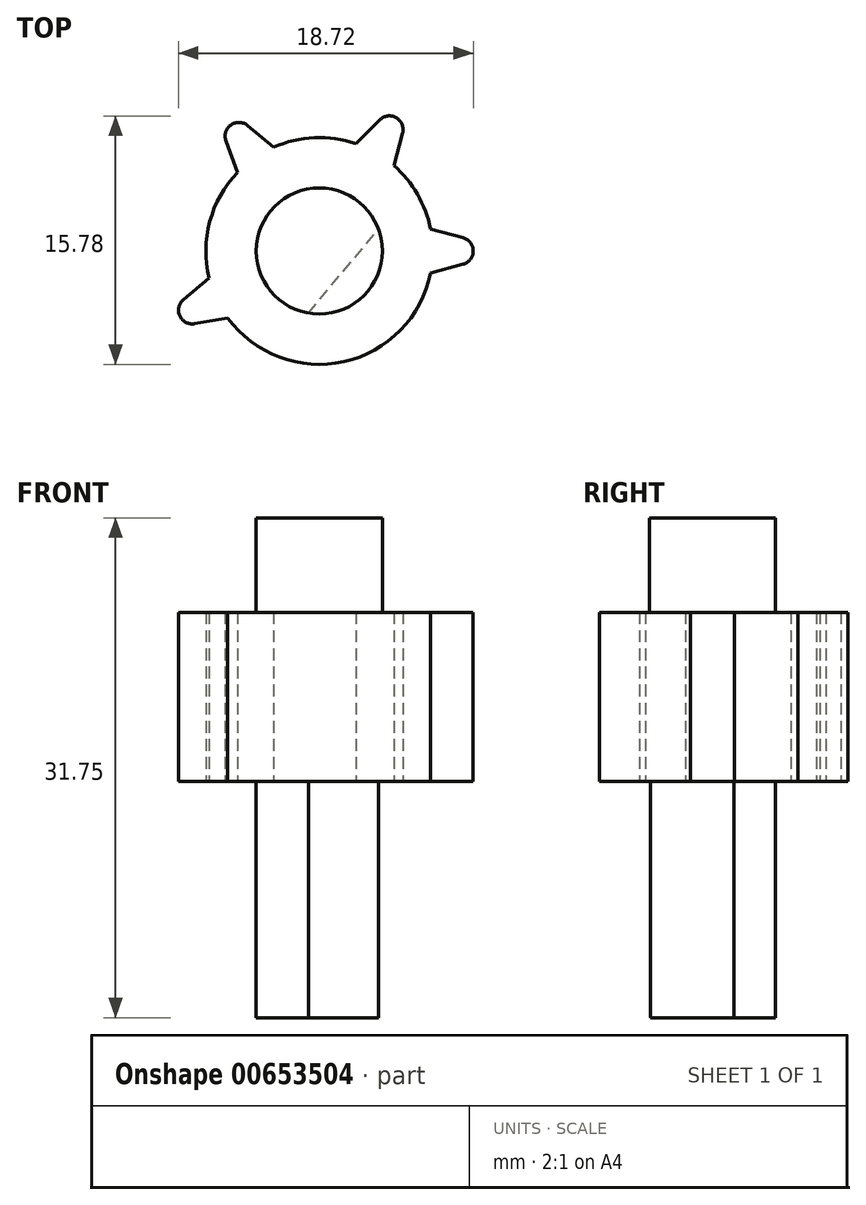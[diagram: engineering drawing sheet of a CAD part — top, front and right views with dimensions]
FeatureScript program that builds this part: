
annotation { "Feature Type Name" : "Feature", "Feature Type Description" : "" }
export const myFeature = defineFeature(function(context is Context, id is Id, definition is map)
    precondition{}
    {
        {
            var Q0;
            Q0=qCreatedBy(makeId("Top.planeOp"),FACE);
            var sketch = newSketch(context, id + "F0", { "sketchPlane" : qUnion([Q0])});
            skCircle(sketch, "E0", {"center": v(0, 0) * mm, "radius": 7.2 * mm});
            skLineSegment(sketch, "E1", {"start": v(0, 0) * mm, "end": v(-8.07, -3.76) * mm});
            skLineSegment(sketch, "E2", {"start": v(0, 0) * mm, "end": v(8.9, 0) * mm});
            skLineSegment(sketch, "E3", {"start": v(0, 0) * mm, "end": v(4.45, 7.7) * mm});
            skLineSegment(sketch, "E4", {"start": v(0, 0) * mm, "end": v(-5.1, 7.3) * mm});
            skCircle(sketch, "E5", {"center": v(-5.1, 7.3) * mm, "radius": 0.88 * mm});
            skCircle(sketch, "E6", {"center": v(4.45, 7.7) * mm, "radius": 0.88 * mm});
            skCircle(sketch, "E7", {"center": v(8.9, 0) * mm, "radius": 0.88 * mm});
            skLineSegment(sketch, "E8", {"start": v(4.45, 7.7) * mm, "end": v(5.2, 7.27) * mm, "construction": true});
            skLineSegment(sketch, "E9", {"start": v(4.45, 7.7) * mm, "end": v(3.7, 8.15) * mm, "construction": true});
            skLineSegment(sketch, "E10", {"start": v(-5.1, 7.3) * mm, "end": v(-4.39, 7.8) * mm, "construction": true});
            skLineSegment(sketch, "E11", {"start": v(-5.1, 7.3) * mm, "end": v(-5.82, 6.79) * mm, "construction": true});
            skLineSegment(sketch, "E12", {"start": v(-5.1, 7.3) * mm, "end": v(-4.54, 7.96) * mm, "construction": true});
            skLineSegment(sketch, "E13", {"start": v(-5.1, 7.3) * mm, "end": v(-5.93, 7) * mm, "construction": true});
            skLineSegment(sketch, "E14", {"start": v(8.9, 0) * mm, "end": v(8.9, -0.88) * mm, "construction": true});
            skLineSegment(sketch, "E15", {"start": v(8.9, 0) * mm, "end": v(8.9, 0.88) * mm, "construction": true});
            skLineSegment(sketch, "E16", {"start": v(8.9, 0) * mm, "end": v(9.13, 0.85) * mm});
            skLineSegment(sketch, "E17", {"start": v(8.9, 0) * mm, "end": v(9.13, -0.85) * mm});
            skLineSegment(sketch, "E18", {"start": v(4.45, 7.7) * mm, "end": v(3.83, 8.33) * mm});
            skLineSegment(sketch, "E19", {"start": v(4.45, 7.7) * mm, "end": v(5.3, 7.48) * mm});
            skLineSegment(sketch, "E20", {"start": v(-5.93, 7) * mm, "end": v(-5.2, 4.98) * mm});
            skLineSegment(sketch, "E21", {"start": v(-4.54, 7.96) * mm, "end": v(-2.9, 6.59) * mm});
            skLineSegment(sketch, "E22", {"start": v(3.83, 8.33) * mm, "end": v(2.32, 6.82) * mm});
            skLineSegment(sketch, "E23", {"start": v(5.3, 7.48) * mm, "end": v(4.74, 5.42) * mm});
            skLineSegment(sketch, "E24", {"start": v(9.13, 0.85) * mm, "end": v(7.06, 1.4) * mm});
            skLineSegment(sketch, "E25", {"start": v(9.13, -0.85) * mm, "end": v(7.06, -1.4) * mm});
            skCircle(sketch, "E26", {"center": v(-8.07, -3.76) * mm, "radius": 0.88 * mm});
            skLineSegment(sketch, "E27", {"start": v(-8.07, -3.76) * mm, "end": v(-8.44, -2.97) * mm, "construction": true});
            skLineSegment(sketch, "E28", {"start": v(-8.07, -3.76) * mm, "end": v(-7.7, -4.55) * mm, "construction": true});
            skLineSegment(sketch, "E29", {"start": v(-8.07, -3.76) * mm, "end": v(-7.91, -4.62) * mm, "construction": true});
            skLineSegment(sketch, "E30", {"start": v(-8.07, -3.76) * mm, "end": v(-8.63, -3.1) * mm, "construction": true});
            skLineSegment(sketch, "E31", {"start": v(-8.63, -3.1) * mm, "end": v(-7, -1.72) * mm});
            skLineSegment(sketch, "E32", {"start": v(-7.91, -4.62) * mm, "end": v(-5.81, -4.25) * mm});
            skSolve(sketch);
        }
        {
            var Q0;
            Q0 = qSketchRegion(id + "F0", true);
            extrude(context, id + "F1", {"entities" : qUnion([Q0]), "depth" : 10.75 * mm, "offsetDistance" : 25 * mm});
        }
        {
            var Q0;
            Q0=makeQuery(id+"F1.opExtrude","CAP_FACE",FACE,{"disambiguationData":[OSD([sQuery(id+"F0.wireOp",EDGE,"E0"),sQuery(id+"F0.wireOp",EDGE,"E5"),sQuery(id+"F0.wireOp",EDGE,"E6"),sQuery(id+"F0.wireOp",EDGE,"E7"),sQuery(id+"F0.wireOp",EDGE,"E20"),sQuery(id+"F0.wireOp",EDGE,"E21"),sQuery(id+"F0.wireOp",EDGE,"E22"),sQuery(id+"F0.wireOp",EDGE,"E23"),sQuery(id+"F0.wireOp",EDGE,"E24"),sQuery(id+"F0.wireOp",EDGE,"E25"),sQuery(id+"F0.wireOp",EDGE,"E26"),sQuery(id+"F0.wireOp",EDGE,"E31"),sQuery(id+"F0.wireOp",EDGE,"E32")])],"isStart":false});
            var sketch = newSketch(context, id + "F2", { "sketchPlane" : qUnion([Q0])});
            skCircle(sketch, "E33", {"center": v(0, 0) * mm, "radius": 4 * mm});
            skSolve(sketch);
        }
        {
            var Q0;
            Q0 = qSketchRegion(id + "F2", true);
            extrude(context, id + "F3", {"entities" : qUnion([Q0]), "operationType" : NewBodyOperationType.ADD, "depth" : 6 * mm, "offsetDistance" : 25 * mm});
        }
        {
            var Q0;
            Q0=makeQuery(id+"F1.opExtrude","CAP_FACE",FACE,{"disambiguationData":[OSD([sQuery(id+"F0.wireOp",EDGE,"E0"),sQuery(id+"F0.wireOp",EDGE,"E5"),sQuery(id+"F0.wireOp",EDGE,"E6"),sQuery(id+"F0.wireOp",EDGE,"E7"),sQuery(id+"F0.wireOp",EDGE,"E20"),sQuery(id+"F0.wireOp",EDGE,"E21"),sQuery(id+"F0.wireOp",EDGE,"E22"),sQuery(id+"F0.wireOp",EDGE,"E23"),sQuery(id+"F0.wireOp",EDGE,"E24"),sQuery(id+"F0.wireOp",EDGE,"E25"),sQuery(id+"F0.wireOp",EDGE,"E26"),sQuery(id+"F0.wireOp",EDGE,"E31"),sQuery(id+"F0.wireOp",EDGE,"E32")])],"isStart":true});
            var sketch = newSketch(context, id + "F4", { "sketchPlane" : qUnion([Q0])});
            skArc(sketch, "E34", {"start": v(-0.7, 3.94) * mm, "mid": v(-3.06, -2.57) * mm, "end": v(3.76, -1.37) * mm});
            skLineSegment(sketch, "E35", {"start": v(0, 0) * mm, "end": v(2.61, 0) * mm, "construction": true});
            skLineSegment(sketch, "E36", {"start": v(2.61, 0) * mm, "end": v(-0.95, 4.25) * mm, "construction": true});
            skLineSegment(sketch, "E37", {"start": v(0, 0) * mm, "end": v(1.53, 1.29) * mm});
            skLineSegment(sketch, "E38", {"start": v(-0.7, 3.94) * mm, "end": v(3.76, -1.37) * mm});
            skSolve(sketch);
        }
        {
            var Q0;
            Q0 = qSketchRegion(id + "F4", true);
            extrude(context, id + "F5", {"entities" : qUnion([Q0]), "operationType" : NewBodyOperationType.ADD, "depth" : 15 * mm, "offsetDistance" : 25 * mm});
        }
    });
